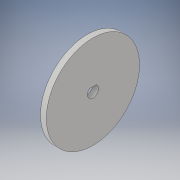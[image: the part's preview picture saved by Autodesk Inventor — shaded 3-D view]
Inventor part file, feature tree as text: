
AUTODESK INVENTOR PART (.ipt)
format: ipt  version: 2019 (Build 230136000, 136)  size: 101,888 bytes
history: native  units: in
note: dims shown in document units (in); Inventor stores cm internally (conversion verified against a paired STEP export)
features: extrude x2, sketch x2
ambient origin geometry x8: Origin, YZ Plane, XZ Plane, XY Plane, X Axis, Y Axis, Z Axis, Center Point
bodies: Solid1 (feature_tree)
feature tree (4):
  extrude  "Extrusion1"  Depth=0.125in TaperAngle=0.0deg
  extrude  "Extrusion2"  Depth=0.125in
  sketch  "Sketch1"  dims[d0=2.0in d1=0.125in d2=0.0in]
  sketch  "Sketch2"  dims[d3=0.2362in d4=0.2126in d5=0.125in d6=0.0in]
